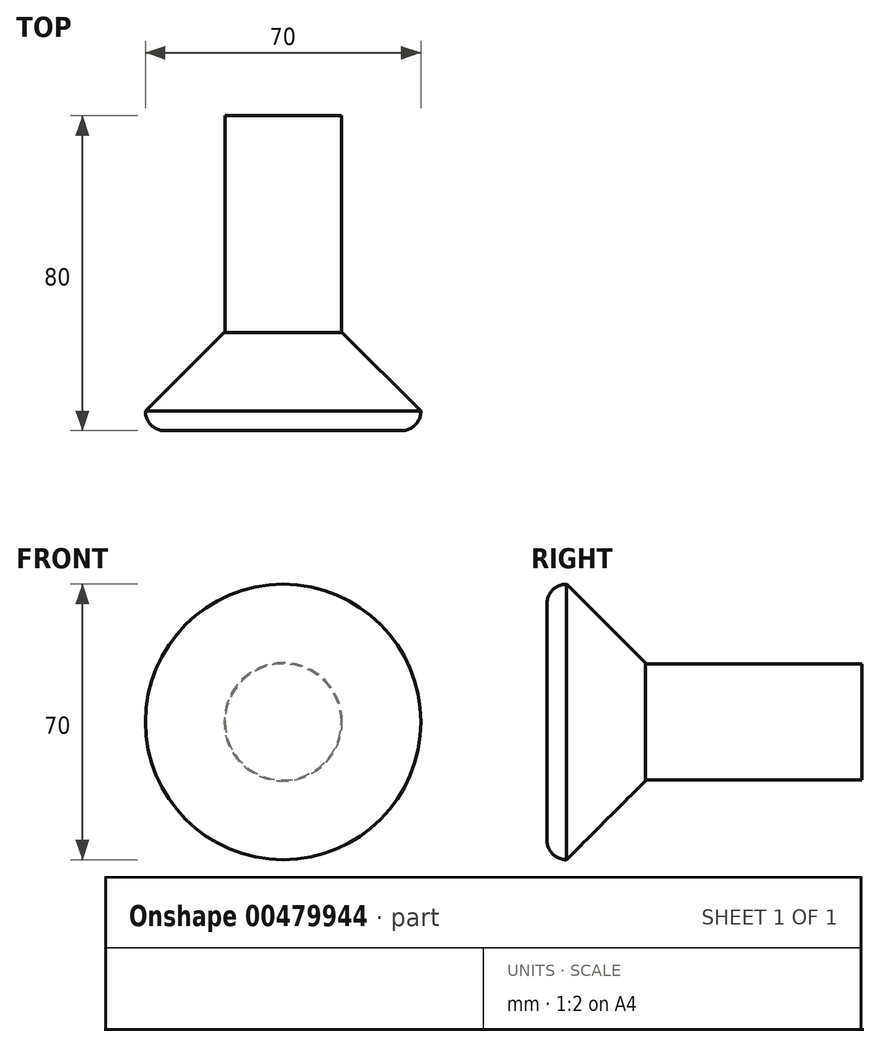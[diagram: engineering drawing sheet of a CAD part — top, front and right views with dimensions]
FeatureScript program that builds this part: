
annotation { "Feature Type Name" : "Feature", "Feature Type Description" : "" }
export const myFeature = defineFeature(function(context is Context, id is Id, definition is map)
    precondition{}
    {
        {
            var Q0;
            Q0=qCreatedBy(makeId("Front.planeOp"),FACE);
            var sketch = newSketch(context, id + "F0", { "sketchPlane" : qUnion([Q0])});
            skCircle(sketch, "E0", {"center": v(0, 0) * mm, "radius": 35 * mm});
            skSolve(sketch);
        }
        {
            var Q0;
            Q0 = qSketchRegion(id + "F0", true);
            extrude(context, id + "F1", {"entities" : qUnion([Q0]), "endBound" : BoundingType.SYMMETRIC, "depth" : 25 * mm});
        }
        {
            var Q0;
            Q0=makeQuery(id+"F1.opExtrude","CAP_FACE",FACE,{"disambiguationData":[OSD([sQuery(id+"F0.wireOp",EDGE,"E0")])],"isStart":false});
            fillet(context, id + "F2", {"entities" : qUnion([Q0]), "radius" : 5 * mm, "tangentPropagation" : true, "allowEdgeOverflow" : false});
        }
        {
            var Q0;
            Q0=makeQuery(id+"F1.opExtrude","CAP_EDGE",EDGE,{"disambiguationData":[OSD([sQuery(id+"F0.wireOp",EDGE,"E0")])],"isStart":true});
            chamfer(context, id + "F3", {"entities" : qUnion([Q0]), "width" : 20 * mm, "tangentPropagation" : true});
        }
        {
            var Q0;
            Q0=makeQuery(id+"F1.opExtrude","CAP_FACE",FACE,{"disambiguationData":[OSD([sQuery(id+"F0.wireOp",EDGE,"E0")])],"isStart":true});
            var sketch = newSketch(context, id + "F4", { "sketchPlane" : qUnion([Q0])});
            skCircle(sketch, "E1", {"center": v(0, 0) * mm, "radius": 14.77 * mm});
            skSolve(sketch);
        }
        {
            var Q0;
            Q0 = qSketchRegion(id + "F4", true);
            extrude(context, id + "F5", {"entities" : qUnion([Q0]), "operationType" : NewBodyOperationType.ADD, "depth" : 55 * mm});
        }
    });
